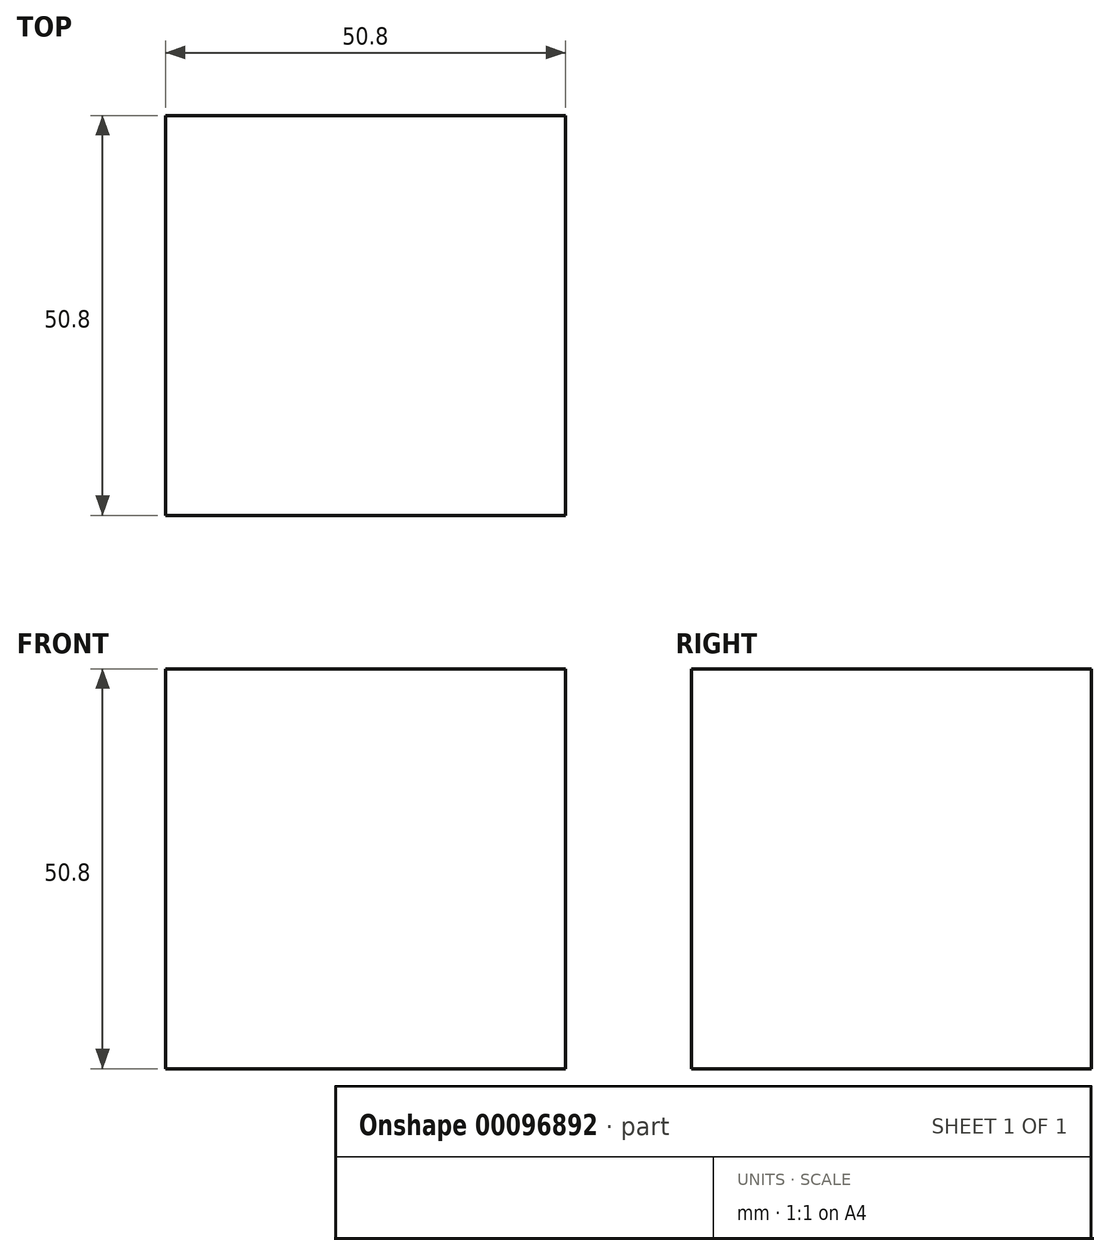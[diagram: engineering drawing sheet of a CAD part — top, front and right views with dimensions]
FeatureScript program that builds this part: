
annotation { "Feature Type Name" : "Feature", "Feature Type Description" : "" }
export const myFeature = defineFeature(function(context is Context, id is Id, definition is map)
    precondition{}
    {
        {
            var Q0;
            Q0=qCreatedBy(makeId("Front.planeOp"),FACE);
            var sketch = newSketch(context, id + "F0", { "sketchPlane" : qUnion([Q0])});
            skLineSegment(sketch, "E0.bottom", {"start": v(25.4, -25.4) * mm, "end": v(-25.4, -25.4) * mm});
            skLineSegment(sketch, "E0.top", {"start": v(25.4, 25.4) * mm, "end": v(-25.4, 25.4) * mm});
            skLineSegment(sketch, "E0.left", {"start": v(25.4, -25.4) * mm, "end": v(25.4, 25.4) * mm});
            skLineSegment(sketch, "E0.right", {"start": v(-25.4, -25.4) * mm, "end": v(-25.4, 25.4) * mm});
            skPoint(sketch, "E0.middle", {"position": v(0, 0) * mm});
            skSolve(sketch);
        }
        {
            var Q0;
            Q0=makeQuery(id+"F0.imprint","IMPRINT",FACE,{"disambiguationData":[TD([[makeQuery(id+"F0.imprint","IMPRINT",EDGE,{"derivedFrom":sQuery(id+"F0.wireOp",EDGE,"E0.bottom")}),-1.0]])]});
            extrude(context, id + "F1", {"entities" : qUnion([Q0]), "depth" : 50.8 * mm});
        }
    });
